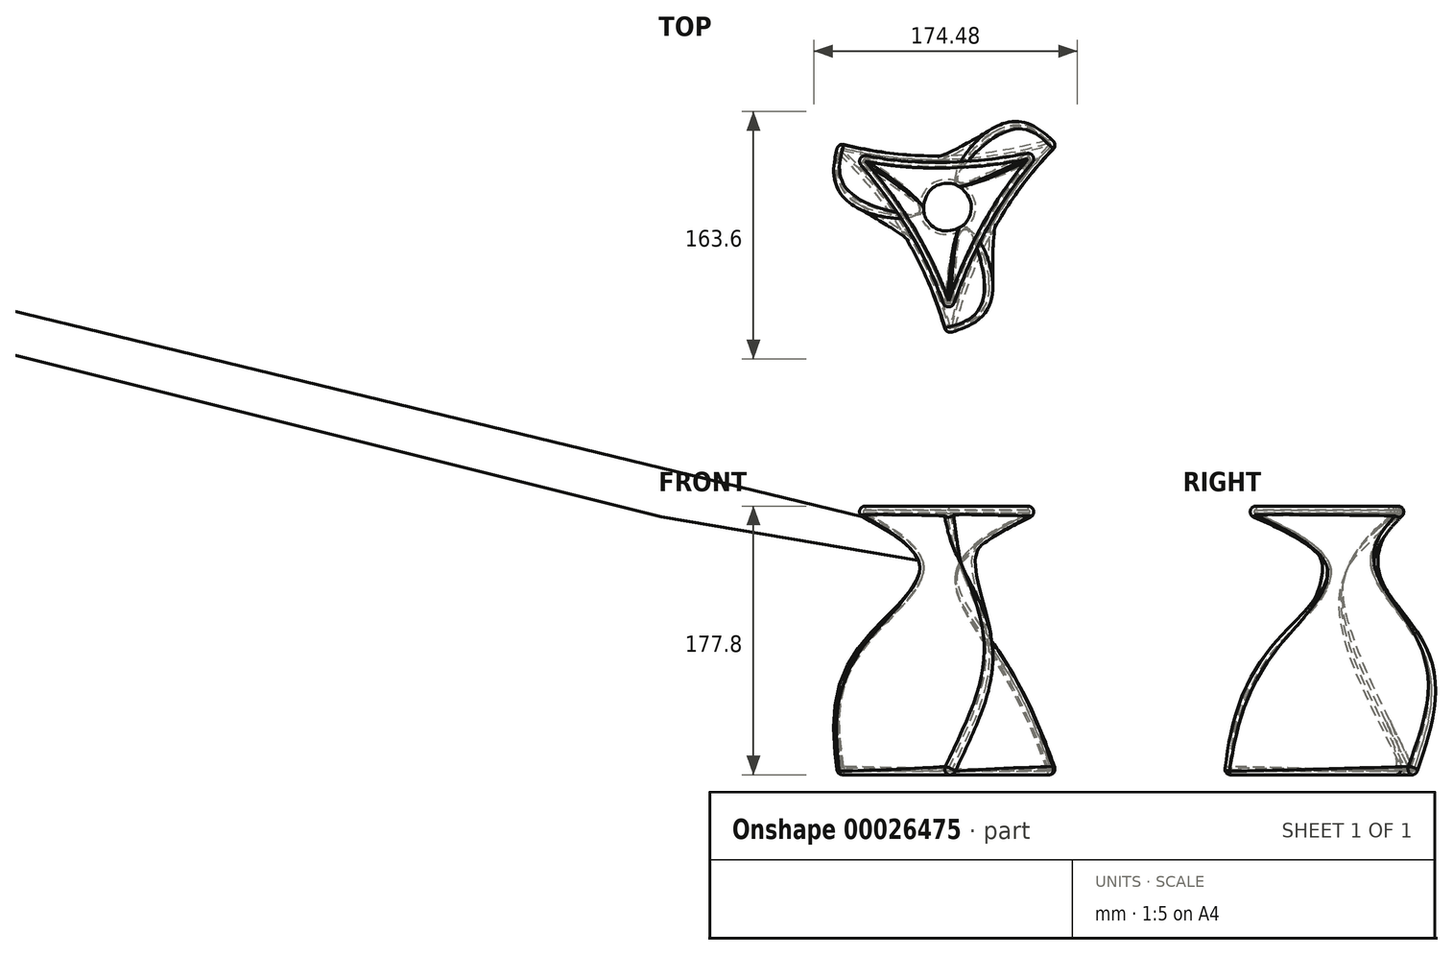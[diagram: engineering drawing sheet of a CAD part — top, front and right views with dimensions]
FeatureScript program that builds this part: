
annotation { "Feature Type Name" : "Feature", "Feature Type Description" : "" }
export const myFeature = defineFeature(function(context is Context, id is Id, definition is map)
    precondition{}
    {
        {
            var Q0;
            Q0=qCreatedBy(makeId("Top.planeOp"),FACE);
            var sketch = newSketch(context, id + "F0", { "sketchPlane" : qUnion([Q0])});
            skCircle(sketch, "E0.cCircle", {"center": v(0, 0) * mm, "radius": 50.55 * mm, "construction": true});
            skPoint(sketch, "E0.0.midPoint", {"position": v(43.8, -25.24) * mm});
            skArc(sketch, "E1", {"start": v(-87.59, 50.48) * mm, "mid": v(-0.03, 34.05) * mm, "end": v(87.5, 50.61) * mm});
            skArc(sketch, "E2.1.0", {"start": v(0.08, -101.1) * mm, "mid": v(-29.48, -17.05) * mm, "end": v(-87.59, 50.48) * mm});
            skArc(sketch, "E2.2.0", {"start": v(87.5, 50.61) * mm, "mid": v(29.5, -17) * mm, "end": v(0.08, -101.1) * mm});
            skSolve(sketch);
        }
        {
            var Q0;
            Q0=qCreatedBy(makeId("Top.planeOp"),FACE);
            cPlane(context, id + "F1", {"entities" : qUnion([Q0]), "cplaneType" : CPlaneType.OFFSET, "offset" : 177.8 * mm, "width" : 152.4 * mm, "height" : 152.4 * mm});
        }
        {
            var Q0;
            Q0=qCreatedBy(id+"F1.planeOp",FACE);
            var sketch = newSketch(context, id + "F2", { "sketchPlane" : qUnion([Q0])});
            skArc(sketch, "E3", {"start": v(77.06, 44.32) * mm, "mid": v(28.49, -16.51) * mm, "end": v(-0.15, -88.9) * mm});
            skArc(sketch, "E4.1.0", {"start": v(-76.92, 44.58) * mm, "mid": v(0.05, 32.93) * mm, "end": v(77.06, 44.32) * mm});
            skArc(sketch, "E4.2.0", {"start": v(-0.15, -88.9) * mm, "mid": v(-28.54, -16.42) * mm, "end": v(-76.92, 44.58) * mm});
            skPoint(sketch, "E4.center", {"position": v(0, 0) * mm});
            skSolve(sketch);
        }
        {
            var Q0;
            Q0=qCreatedBy(makeId("Top.planeOp"),FACE);
            cPlane(context, id + "F3", {"entities" : qUnion([Q0]), "cplaneType" : CPlaneType.OFFSET, "offset" : 88.9 * mm, "width" : 152.4 * mm, "height" : 152.4 * mm});
        }
        {
            var Q0;
            Q0=qCreatedBy(id+"F3.planeOp",FACE);
            var sketch = newSketch(context, id + "F4", { "sketchPlane" : qUnion([Q0])});
            skCircle(sketch, "E5.cCircle", {"center": v(0, 0) * mm, "radius": 29.33 * mm, "construction": true});
            skLineSegment(sketch, "E5.0", {"start": v(29.33, 50.8) * mm, "end": v(29.33, -50.8) * mm});
            skLineSegment(sketch, "E5.1", {"start": v(29.33, -50.8) * mm, "end": v(-58.66, 0) * mm});
            skLineSegment(sketch, "E5.2", {"start": v(-58.66, 0) * mm, "end": v(29.33, 50.8) * mm});
            skPoint(sketch, "E5.0.midPoint", {"position": v(29.33, 0) * mm});
            skSolve(sketch);
        }
        {
            var Q0;
            Q0=qCreatedBy(id+"F3.planeOp",FACE);
            cPlane(context, id + "F5", {"entities" : qUnion([Q0]), "cplaneType" : CPlaneType.OFFSET, "offset" : 50.8 * mm, "width" : 152.4 * mm, "height" : 152.4 * mm});
        }
        {
            var Q0;
            Q0=qCreatedBy(id+"F5.planeOp",FACE);
            var sketch = newSketch(context, id + "F6", { "sketchPlane" : qUnion([Q0])});
            skCircle(sketch, "E6", {"center": v(0, 0) * mm, "radius": 18.5 * mm});
            skSolve(sketch);
        }
        {
            var Q0;
            Q0=makeQuery(id+"F0.imprint","IMPRINT",FACE,{"disambiguationData":[TD([[makeQuery(id+"F0.imprint","IMPRINT",EDGE,{"derivedFrom":sQuery(id+"F0.wireOp",EDGE,"E1")}),-1.0]])]});
            var Q1;
            Q1=makeQuery(id+"F4.imprint","IMPRINT",FACE,{"disambiguationData":[TD([[makeQuery(id+"F4.imprint","IMPRINT",EDGE,{"derivedFrom":sQuery(id+"F4.wireOp",EDGE,"E5.0")}),-1.0]])]});
            var Q2;
            Q2=makeQuery(id+"F6.imprint","IMPRINT",FACE,{"disambiguationData":[TD([[makeQuery(id+"F6.imprint","IMPRINT",EDGE,{"derivedFrom":sQuery(id+"F6.wireOp",EDGE,"E6")}),1.0]])]});
            var Q3;
            Q3=makeQuery(id+"F2.imprint","IMPRINT",FACE,{"disambiguationData":[TD([[makeQuery(id+"F2.imprint","IMPRINT",EDGE,{"derivedFrom":sQuery(id+"F2.wireOp",EDGE,"E3")}),-1.0]])]});
            loft(context, id + "F7", {"sheetProfilesArray" : [{ "sheetProfileEntities" : qUnion([Q0]) }, { "sheetProfileEntities" : qUnion([Q1]) }, { "sheetProfileEntities" : qUnion([Q2]) }, { "sheetProfileEntities" : qUnion([Q3]) }]});
        }
        {
            var Q0;
            {var subQ0=sQuery(id+"F0.wireOp",EDGE,"E1");var subQ1=sQuery(id+"F0.wireOp",EDGE,"E2.1.0");var subQ2=sQuery(id+"F0.wireOp",EDGE,"E2.2.0");var subQ3=sQuery(id+"F4.wireOp",EDGE,"E5.0");var subQ4=sQuery(id+"F4.wireOp",EDGE,"E5.1");var subQ5=sQuery(id+"F4.wireOp",EDGE,"E5.2");Q0=makeQuery(id+"F7.opLoft","SWEPT_FACE",FACE,{"disambiguationData":[OSD([subQ0,subQ1,subQ2,subQ3,subQ4,subQ5]),TDD([makeQuery(id+"F0.imprint","INTERSECT",VERTEX,{"derivedFrom":[subQ0,subQ1]}),makeQuery(id+"F0.imprint","INTERSECT",VERTEX,{"derivedFrom":[subQ1,subQ2]}),makeQuery(id+"F0.imprint","IMPRINT",EDGE,{"derivedFrom":subQ1}),makeQuery(id+"F4.imprint","INTERSECT",VERTEX,{"derivedFrom":[subQ3,subQ4]}),makeQuery(id+"F4.imprint","INTERSECT",VERTEX,{"derivedFrom":[subQ4,subQ5]}),makeQuery(id+"F4.imprint","IMPRINT",EDGE,{"derivedFrom":subQ4})])]});}
            var Q1;
            {var subQ0=sQuery(id+"F0.wireOp",EDGE,"E1");var subQ1=sQuery(id+"F0.wireOp",EDGE,"E2.1.0");var subQ2=sQuery(id+"F0.wireOp",EDGE,"E2.2.0");var subQ3=sQuery(id+"F4.wireOp",EDGE,"E5.0");var subQ4=sQuery(id+"F4.wireOp",EDGE,"E5.1");var subQ5=sQuery(id+"F4.wireOp",EDGE,"E5.2");Q1=makeQuery(id+"F7.opLoft","SWEPT_FACE",FACE,{"disambiguationData":[OSD([subQ0,subQ1,subQ2,subQ3,subQ4,subQ5]),TDD([makeQuery(id+"F0.imprint","INTERSECT",VERTEX,{"derivedFrom":[subQ0,subQ2]}),makeQuery(id+"F0.imprint","INTERSECT",VERTEX,{"derivedFrom":[subQ1,subQ2]}),makeQuery(id+"F0.imprint","IMPRINT",EDGE,{"derivedFrom":subQ2}),makeQuery(id+"F4.imprint","INTERSECT",VERTEX,{"derivedFrom":[subQ3,subQ5]}),makeQuery(id+"F4.imprint","INTERSECT",VERTEX,{"derivedFrom":[subQ3,subQ4]}),makeQuery(id+"F4.imprint","IMPRINT",EDGE,{"derivedFrom":subQ3})])]});}
            var Q2;
            {var subQ0=sQuery(id+"F0.wireOp",EDGE,"E1");var subQ1=sQuery(id+"F0.wireOp",EDGE,"E2.1.0");var subQ2=sQuery(id+"F0.wireOp",EDGE,"E2.2.0");var subQ3=sQuery(id+"F4.wireOp",EDGE,"E5.0");var subQ4=sQuery(id+"F4.wireOp",EDGE,"E5.1");var subQ5=sQuery(id+"F4.wireOp",EDGE,"E5.2");Q2=makeQuery(id+"F7.opLoft","SWEPT_FACE",FACE,{"disambiguationData":[OSD([subQ0,subQ1,subQ2,subQ3,subQ4,subQ5]),TDD([makeQuery(id+"F0.imprint","INTERSECT",VERTEX,{"derivedFrom":[subQ0,subQ1]}),makeQuery(id+"F0.imprint","INTERSECT",VERTEX,{"derivedFrom":[subQ0,subQ2]}),makeQuery(id+"F0.imprint","IMPRINT",EDGE,{"derivedFrom":subQ0}),makeQuery(id+"F4.imprint","INTERSECT",VERTEX,{"derivedFrom":[subQ3,subQ5]}),makeQuery(id+"F4.imprint","INTERSECT",VERTEX,{"derivedFrom":[subQ4,subQ5]}),makeQuery(id+"F4.imprint","IMPRINT",EDGE,{"derivedFrom":subQ5})])]});}
            fillet(context, id + "F8", {"entities" : qUnion([Q0, Q1, Q2]), "radius" : 3.8 * mm, "tangentPropagation" : true, "allowEdgeOverflow" : false});
        }
        {
            var Q0;
            Q0=makeQuery(id+"F7.opLoft","CAP_FACE",FACE,{"disambiguationData":[OSD([makeQuery(id+"F2.imprint","IMPRINT",FACE,{"disambiguationData":[TD([[makeQuery(id+"F2.imprint","IMPRINT",EDGE,{"derivedFrom":sQuery(id+"F2.wireOp",EDGE,"E3")}),-1.0]])]})])],"isStart":true});
            shell(context, id + "F9", {"entities" : qUnion([Q0]), "thickness" : 2.54 * mm});
        }
    });
